# Revit family: Detail-Connection-Steel & Tube-HST Standard Cleat with Bolts-Side_Temp_d2a93984-5e0c-4afc-827f-cb67c6a37e3f
name_source: partatom
category: Detail Items
revit_build: Autodesk Revit 2016 (Build: 20160314_0715(x64)
units: mm (PartAtom-declared; Revit-internal decimal feet)

## family parameters
OmniClass Number = 23.35.20.14.11.14
OmniClass Title = Sheet Metal Roofing
Rotate with component = No
Shared = No

## types (1)
- HST150
    Assembly Code = B1020230
    Beam Size = 152 mm  [stored 0.498688 ft]
    Bolt Row2 Validation = 80 mm  [stored 0.262467 ft]
    CBICode = 3411
    CBIDescription = Structural steelwork
    Description = HST Steel Purlins and Girts are high strength lipped profile sections, providing an economic solution for your building project.
    Height_ANZRS = 150 mm
    Manufacturer = Steel & Tube
    ManufacturerName = Steel & Tube
    ManufacturerURL = http://www.steelandtube.co.nz
    Model = HST150
    ModifiedIssue_ANZRS = 20160520 $
    SpecificationDescription = Steel & Tube Purlins & Girts
    SpecificationReference = 3411ST
    Type Comments = HST Standard Cleat with Bolts-Side
    URL = http://www.steelandtube.co.nz
    Uniclass2015Code = Pr_20_76_51_21
    Uniclass2015Title = Cold-formed galvanized steel sections
    Uniclass2015Version = 2015
    f = 41 mm  [stored 0.134514 ft]
    g = 80 mm  [stored 0.262467 ft]

note: [stored X ft] marks values corroborated as IEEE doubles in the binary element streams (Revit-internal decimal feet)

## geometry (parser evidence)
native form markers: Sweep x2
no freeform markers — native parametric forms only
